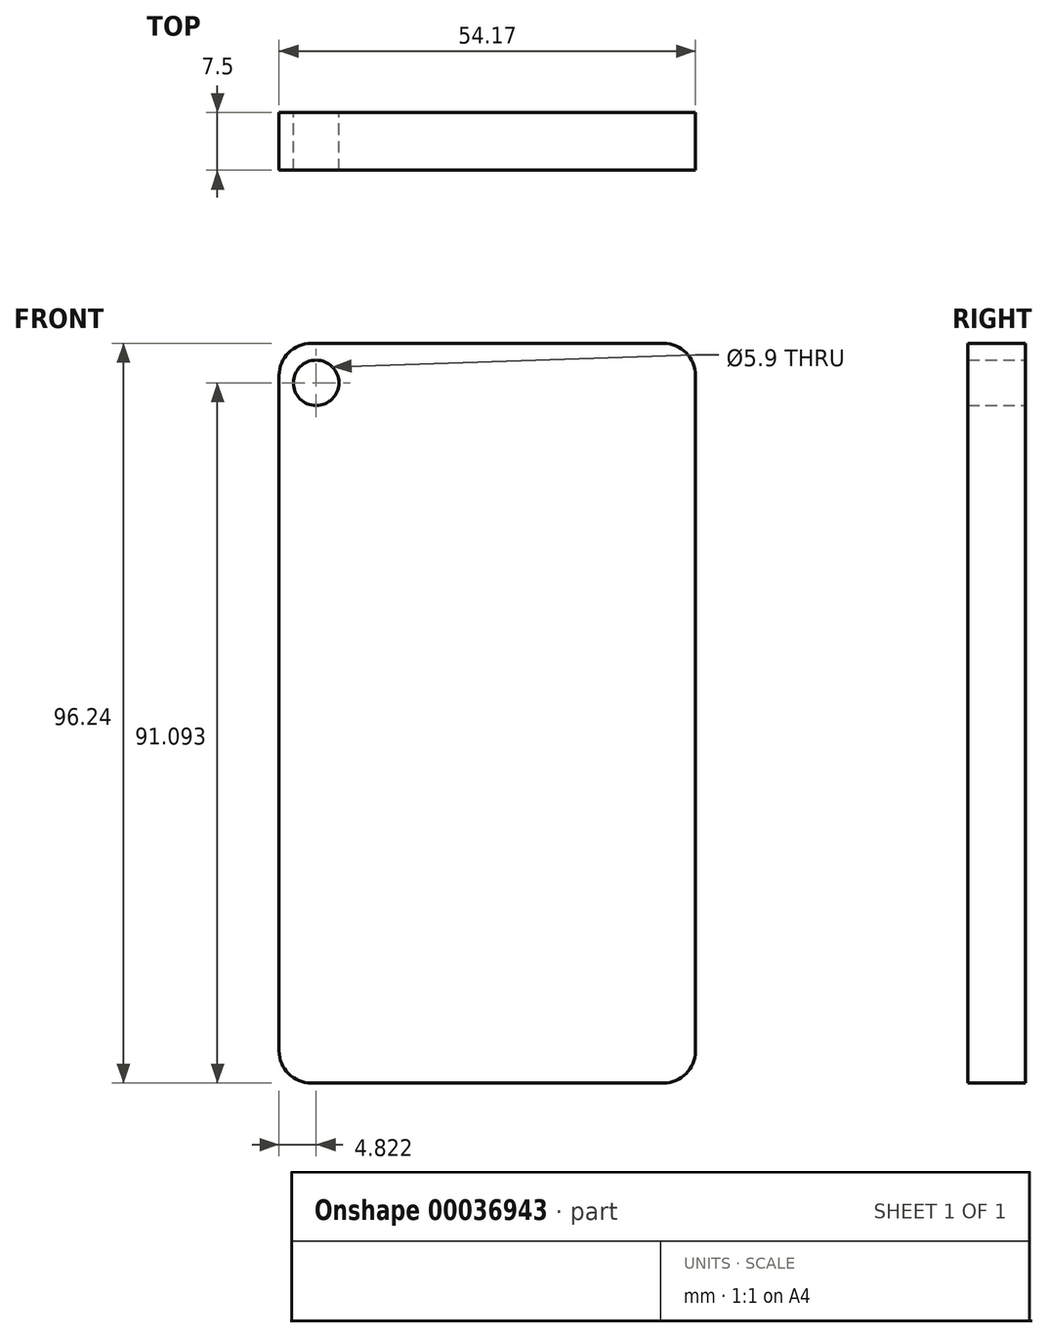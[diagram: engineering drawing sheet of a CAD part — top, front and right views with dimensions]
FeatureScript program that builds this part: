
annotation { "Feature Type Name" : "Feature", "Feature Type Description" : "" }
export const myFeature = defineFeature(function(context is Context, id is Id, definition is map)
    precondition{}
    {
        {
            var Q0;
            Q0=qCreatedBy(makeId("Front.planeOp"),FACE);
            var sketch = newSketch(context, id + "F0", { "sketchPlane" : qUnion([Q0])});
            skLineSegment(sketch, "E0", {"start": v(-25.5, 39.42) * mm, "end": v(28.67, 39.42) * mm});
            skLineSegment(sketch, "E1", {"start": v(28.67, 39.42) * mm, "end": v(28.67, -56.82) * mm});
            skLineSegment(sketch, "E2", {"start": v(28.67, -56.82) * mm, "end": v(-25.5, -56.82) * mm});
            skLineSegment(sketch, "E3", {"start": v(-25.5, -56.82) * mm, "end": v(-25.5, 39.42) * mm});
            skCircle(sketch, "E4", {"center": v(-20.68, 34.27) * mm, "radius": 2.95 * mm});
            skSolve(sketch);
        }
        {
            var Q0;
            Q0=makeQuery(id+"F0.imprint","IMPRINT",FACE,{"disambiguationData":[TD([[makeQuery(id+"F0.imprint","IMPRINT",EDGE,{"derivedFrom":sQuery(id+"F0.wireOp",EDGE,"E0")}),-1.0]])]});
            extrude(context, id + "F1", {"entities" : qUnion([Q0]), "depth" : 7.5 * mm});
        }
        {
            var Q0;
            Q0=makeQuery(id+"F1.opExtrude","SWEPT_EDGE",EDGE,{"disambiguationData":[OSD([sQuery(id+"F0.wireOp",EDGE,"E0"),sQuery(id+"F0.wireOp",EDGE,"E3")])]});
            var Q1;
            Q1=makeQuery(id+"F1.opExtrude","SWEPT_EDGE",EDGE,{"disambiguationData":[OSD([sQuery(id+"F0.wireOp",EDGE,"E2"),sQuery(id+"F0.wireOp",EDGE,"E3")])]});
            var Q2;
            Q2=makeQuery(id+"F1.opExtrude","SWEPT_EDGE",EDGE,{"disambiguationData":[OSD([sQuery(id+"F0.wireOp",EDGE,"E1"),sQuery(id+"F0.wireOp",EDGE,"E2")])]});
            var Q3;
            Q3=makeQuery(id+"F1.opExtrude","SWEPT_EDGE",EDGE,{"disambiguationData":[OSD([sQuery(id+"F0.wireOp",EDGE,"E0"),sQuery(id+"F0.wireOp",EDGE,"E1")])]});
            fillet(context, id + "F2", {"entities" : qUnion([Q0, Q1, Q2, Q3]), "radius" : 4.2 * mm, "tangentPropagation" : true, "allowEdgeOverflow" : false});
        }
    });
